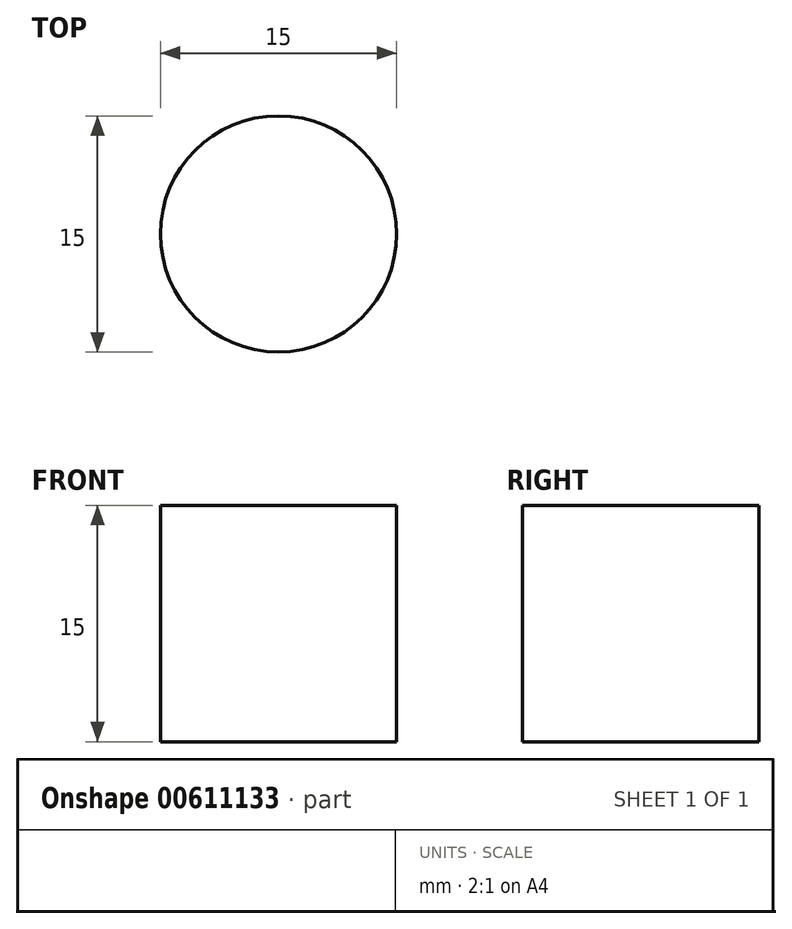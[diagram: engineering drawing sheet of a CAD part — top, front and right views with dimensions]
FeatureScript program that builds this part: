
annotation { "Feature Type Name" : "Feature", "Feature Type Description" : "" }
export const myFeature = defineFeature(function(context is Context, id is Id, definition is map)
    precondition{}
    {
        {
            var Q0;
            Q0=qCreatedBy(makeId("Top.planeOp"),FACE);
            var sketch = newSketch(context, id + "F0", { "sketchPlane" : qUnion([Q0])});
            skCircle(sketch, "E0", {"center": v(0, 0) * mm, "radius": 7.5 * mm});
            skSolve(sketch);
        }
        {
            var Q0;
            Q0=makeQuery(id+"F0.imprint","IMPRINT",FACE,{"disambiguationData":[TD([[makeQuery(id+"F0.imprint","IMPRINT",EDGE,{"derivedFrom":sQuery(id+"F0.wireOp",EDGE,"E0")}),1.0]])]});
            extrude(context, id + "F1", {"entities" : qUnion([Q0]), "depth" : 15 * mm, "offsetDistance" : 25 * mm});
        }
    });
